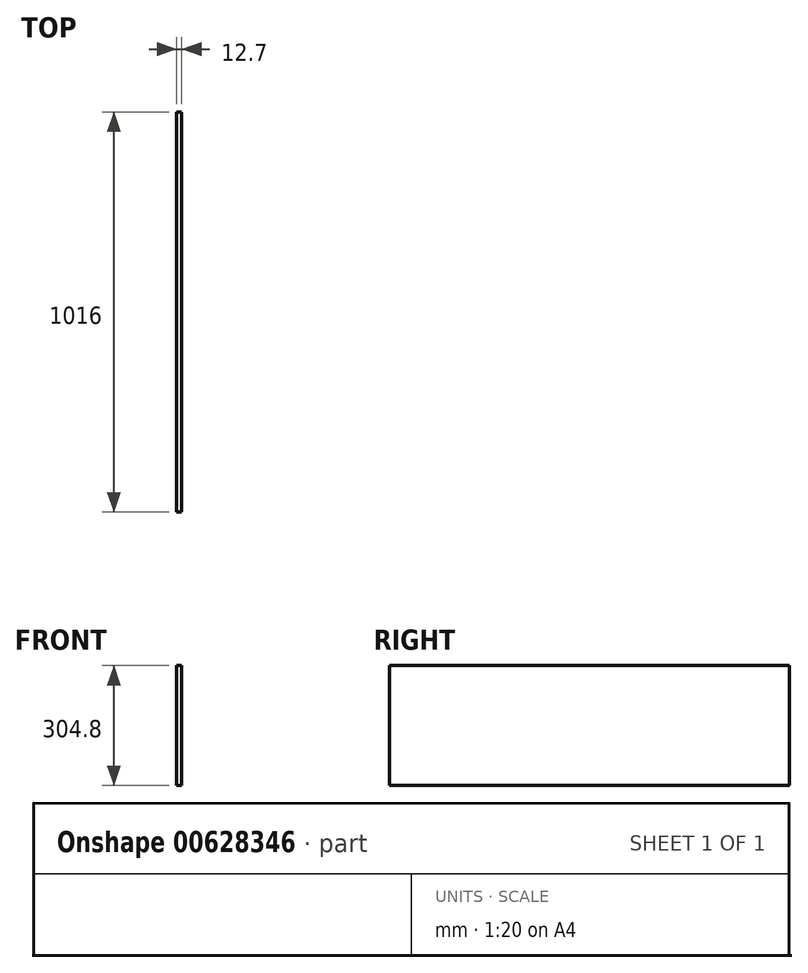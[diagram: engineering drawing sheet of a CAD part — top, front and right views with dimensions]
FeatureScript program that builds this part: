
annotation { "Feature Type Name" : "Feature", "Feature Type Description" : "" }
export const myFeature = defineFeature(function(context is Context, id is Id, definition is map)
    precondition{}
    {
        {
            var Q0;
            Q0=qCreatedBy(makeId("Right.planeOp"),FACE);
            var sketch = newSketch(context, id + "F0", { "sketchPlane" : qUnion([Q0])});
            skLineSegment(sketch, "E0.bottom", {"start": v(0, 0) * mm, "end": v(1016, 0) * mm});
            skLineSegment(sketch, "E0.top", {"start": v(0, 304.8) * mm, "end": v(1016, 304.8) * mm});
            skLineSegment(sketch, "E0.left", {"start": v(0, 0) * mm, "end": v(0, 304.8) * mm});
            skLineSegment(sketch, "E0.right", {"start": v(1016, 0) * mm, "end": v(1016, 304.8) * mm});
            skSolve(sketch);
        }
        {
            var Q0;
            Q0 = qSketchRegion(id + "F0", true);
            extrude(context, id + "F1", {"entities" : qUnion([Q0]), "depth" : 12.7 * mm, "offsetDistance" : 25.4 * mm});
        }
    });
